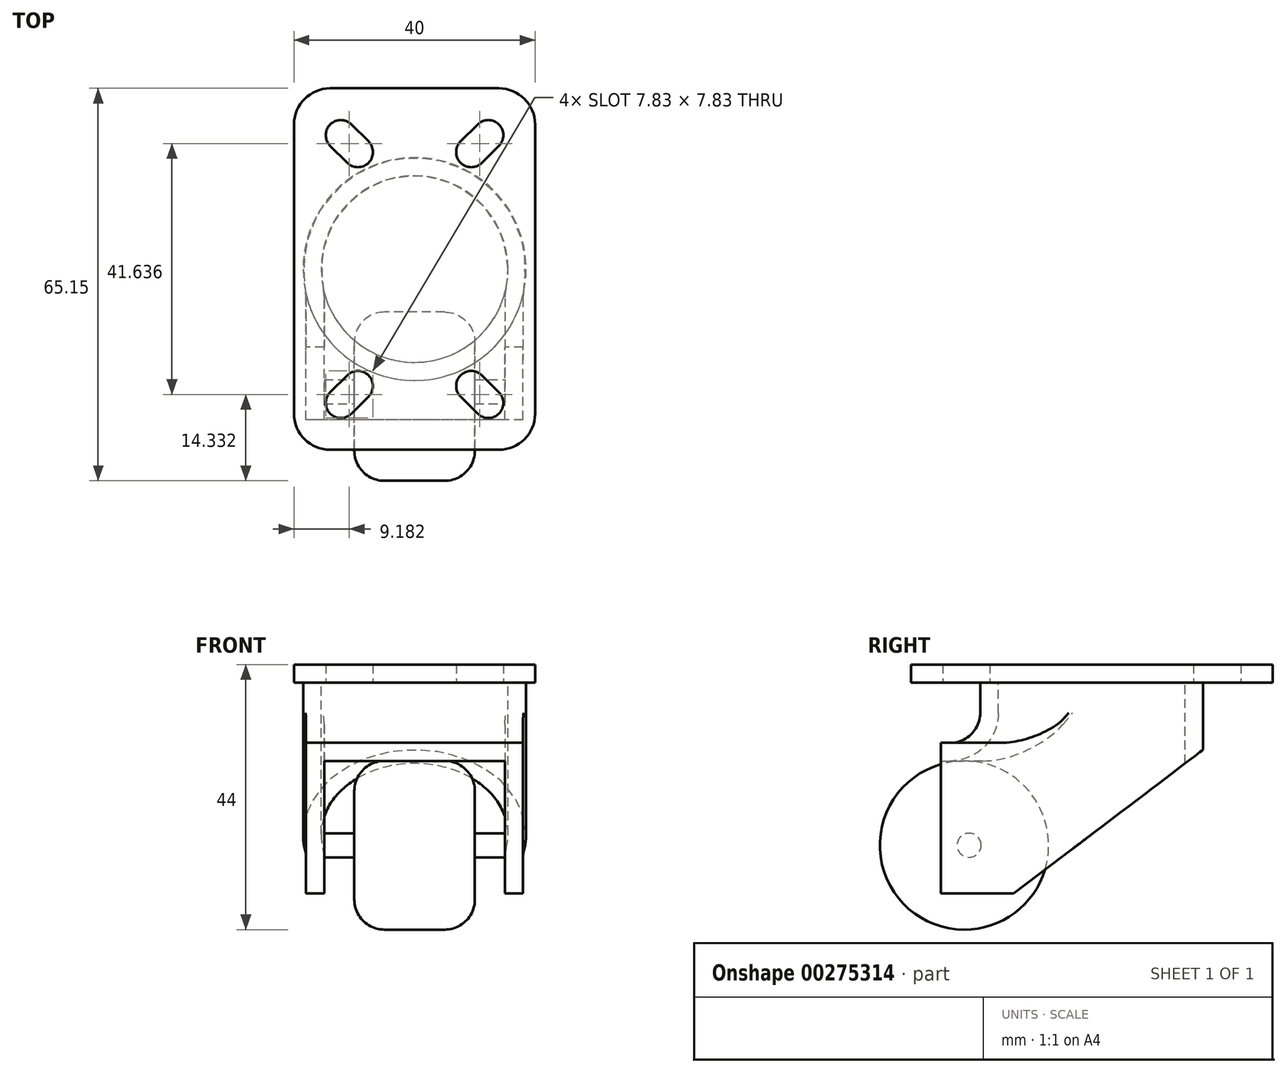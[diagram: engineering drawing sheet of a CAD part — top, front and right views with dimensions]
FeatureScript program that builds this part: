
annotation { "Feature Type Name" : "Feature", "Feature Type Description" : "" }
export const myFeature = defineFeature(function(context is Context, id is Id, definition is map)
    precondition{}
    {
        {
            var Q0;
            Q0=qCreatedBy(makeId("Top.planeOp"),FACE);
            var sketch = newSketch(context, id + "F0", { "sketchPlane" : qUnion([Q0])});
            skLineSegment(sketch, "E0.bottom", {"start": v(14, 30) * mm, "end": v(-14, 30) * mm});
            skLineSegment(sketch, "E0.top", {"start": v(14, -30) * mm, "end": v(-14, -30) * mm});
            skLineSegment(sketch, "E0.left", {"start": v(20, 24) * mm, "end": v(20, -24) * mm});
            skLineSegment(sketch, "E0.right", {"start": v(-20, 24) * mm, "end": v(-20, -24) * mm});
            skPoint(sketch, "E0.middle", {"position": v(0, 0) * mm});
            skPoint(sketch, "E1.visualSharp", {"position": v(-20, 30) * mm});
            skArc(sketch, "E1.filletArc", {"start": v(-14, 30) * mm, "mid": v(-18.24, 28.24) * mm, "end": v(-20, 24) * mm});
            skPoint(sketch, "E2.visualSharp", {"position": v(20, 30) * mm});
            skArc(sketch, "E2.filletArc", {"start": v(20, 24) * mm, "mid": v(18.24, 28.24) * mm, "end": v(14, 30) * mm});
            skPoint(sketch, "E3.visualSharp", {"position": v(-20, -30) * mm});
            skArc(sketch, "E3.filletArc", {"start": v(-20, -24) * mm, "mid": v(-18.24, -28.24) * mm, "end": v(-14, -30) * mm});
            skPoint(sketch, "E4.visualSharp", {"position": v(20, -30) * mm});
            skArc(sketch, "E4.filletArc", {"start": v(14, -30) * mm, "mid": v(18.24, -28.24) * mm, "end": v(20, -24) * mm});
            skLineSegment(sketch, "E5", {"start": v(-14, 24) * mm, "end": v(-14, 24) * mm});
            skLineSegment(sketch, "E6", {"start": v(-14, 20.46) * mm, "end": v(-11.17, 17.64) * mm});
            skLineSegment(sketch, "E7", {"start": v(-10.46, 24) * mm, "end": v(-7.64, 21.17) * mm});
            skLineSegment(sketch, "E8", {"start": v(-7.64, 17.64) * mm, "end": v(-7.64, 17.64) * mm});
            skPoint(sketch, "E9.visualSharp", {"position": v(-15.77, 22.23) * mm});
            skArc(sketch, "E9.filletArc", {"start": v(-14, 24) * mm, "mid": v(-14.73, 22.23) * mm, "end": v(-14, 20.46) * mm});
            skPoint(sketch, "E10.visualSharp", {"position": v(-12.23, 25.77) * mm});
            skArc(sketch, "E10.filletArc", {"start": v(-10.46, 24) * mm, "mid": v(-12.23, 24.73) * mm, "end": v(-14, 24) * mm});
            skPoint(sketch, "E11.visualSharp", {"position": v(-5.87, 19.4) * mm});
            skArc(sketch, "E11.filletArc", {"start": v(-7.64, 17.64) * mm, "mid": v(-6.9, 19.4) * mm, "end": v(-7.64, 21.17) * mm});
            skPoint(sketch, "E12.visualSharp", {"position": v(-9.4, 15.87) * mm});
            skArc(sketch, "E12.filletArc", {"start": v(-11.17, 17.64) * mm, "mid": v(-9.4, 16.9) * mm, "end": v(-7.64, 17.64) * mm});
            skLineSegment(sketch, "E13.MirrorCS", {"start": v(10.46, 24) * mm, "end": v(7.64, 21.17) * mm});
            skArc(sketch, "E14.MirrorCS", {"start": v(7.64, 17.64) * mm, "mid": v(6.9, 19.4) * mm, "end": v(7.64, 21.17) * mm});
            skArc(sketch, "E15.MirrorCS", {"start": v(11.17, 17.64) * mm, "mid": v(9.4, 16.9) * mm, "end": v(7.64, 17.64) * mm});
            skLineSegment(sketch, "E16.MirrorCS", {"start": v(14, 20.46) * mm, "end": v(11.17, 17.64) * mm});
            skArc(sketch, "E17.MirrorCS", {"start": v(14, 24) * mm, "mid": v(14.73, 22.23) * mm, "end": v(14, 20.46) * mm});
            skArc(sketch, "E18.MirrorCS", {"start": v(10.46, 24) * mm, "mid": v(12.23, 24.73) * mm, "end": v(14, 24) * mm});
            skArc(sketch, "E19.MirrorCS", {"start": v(11.17, -17.64) * mm, "mid": v(9.4, -16.9) * mm, "end": v(7.64, -17.64) * mm});
            skArc(sketch, "E20.MirrorCS", {"start": v(7.64, -17.64) * mm, "mid": v(6.9, -19.4) * mm, "end": v(7.64, -21.17) * mm});
            skLineSegment(sketch, "E21.MirrorCS", {"start": v(10.46, -24) * mm, "end": v(7.64, -21.17) * mm});
            skArc(sketch, "E22.MirrorCS", {"start": v(14, -24) * mm, "mid": v(14.73, -22.23) * mm, "end": v(14, -20.46) * mm});
            skArc(sketch, "E23.MirrorCS", {"start": v(10.46, -24) * mm, "mid": v(12.23, -24.73) * mm, "end": v(14, -24) * mm});
            skLineSegment(sketch, "E24.MirrorCS", {"start": v(14, -20.46) * mm, "end": v(11.17, -17.64) * mm});
            skArc(sketch, "E25.MirrorCS", {"start": v(-7.64, -17.64) * mm, "mid": v(-6.9, -19.4) * mm, "end": v(-7.64, -21.17) * mm});
            skArc(sketch, "E26.MirrorCS", {"start": v(-11.17, -17.64) * mm, "mid": v(-9.4, -16.9) * mm, "end": v(-7.64, -17.64) * mm});
            skLineSegment(sketch, "E27.MirrorCS", {"start": v(-14, -20.46) * mm, "end": v(-11.17, -17.64) * mm});
            skArc(sketch, "E28.MirrorCS", {"start": v(-14, -24) * mm, "mid": v(-14.73, -22.23) * mm, "end": v(-14, -20.46) * mm});
            skArc(sketch, "E29.MirrorCS", {"start": v(-10.46, -24) * mm, "mid": v(-12.23, -24.73) * mm, "end": v(-14, -24) * mm});
            skLineSegment(sketch, "E30.MirrorCS", {"start": v(-10.46, -24) * mm, "end": v(-7.64, -21.17) * mm});
            skSolve(sketch);
        }
        {
            var Q0;
            Q0=makeQuery(id+"F0.imprint","IMPRINT",FACE,{"disambiguationData":[TD([[makeQuery(id+"F0.imprint","IMPRINT",EDGE,{"derivedFrom":sQuery(id+"F0.wireOp",EDGE,"E0.bottom")}),1.0]])]});
            extrude(context, id + "F1", {"entities" : qUnion([Q0]), "depth" : 3 * mm});
        }
        {
            var Q0;
            Q0=makeQuery(id+"F1.opExtrude","CAP_FACE",FACE,{"disambiguationData":[OSD([sQuery(id+"F0.wireOp",EDGE,"E0.bottom"),sQuery(id+"F0.wireOp",EDGE,"E0.top"),sQuery(id+"F0.wireOp",EDGE,"E0.left"),sQuery(id+"F0.wireOp",EDGE,"E0.right"),sQuery(id+"F0.wireOp",EDGE,"E1.filletArc"),sQuery(id+"F0.wireOp",EDGE,"E2.filletArc"),sQuery(id+"F0.wireOp",EDGE,"E3.filletArc"),sQuery(id+"F0.wireOp",EDGE,"E4.filletArc"),sQuery(id+"F0.wireOp",EDGE,"E6"),sQuery(id+"F0.wireOp",EDGE,"E7"),sQuery(id+"F0.wireOp",EDGE,"E9.filletArc"),sQuery(id+"F0.wireOp",EDGE,"E10.filletArc"),sQuery(id+"F0.wireOp",EDGE,"E11.filletArc"),sQuery(id+"F0.wireOp",EDGE,"E12.filletArc"),sQuery(id+"F0.wireOp",EDGE,"E13.MirrorCS"),sQuery(id+"F0.wireOp",EDGE,"E14.MirrorCS"),sQuery(id+"F0.wireOp",EDGE,"E15.MirrorCS"),sQuery(id+"F0.wireOp",EDGE,"E16.MirrorCS"),sQuery(id+"F0.wireOp",EDGE,"E17.MirrorCS"),sQuery(id+"F0.wireOp",EDGE,"E18.MirrorCS"),sQuery(id+"F0.wireOp",EDGE,"E19.MirrorCS"),sQuery(id+"F0.wireOp",EDGE,"E20.MirrorCS"),sQuery(id+"F0.wireOp",EDGE,"E22.MirrorCS"),sQuery(id+"F0.wireOp",EDGE,"E23.MirrorCS"),sQuery(id+"F0.wireOp",EDGE,"E21.MirrorCS"),sQuery(id+"F0.wireOp",EDGE,"E24.MirrorCS"),sQuery(id+"F0.wireOp",EDGE,"E25.MirrorCS"),sQuery(id+"F0.wireOp",EDGE,"E26.MirrorCS"),sQuery(id+"F0.wireOp",EDGE,"E27.MirrorCS"),sQuery(id+"F0.wireOp",EDGE,"E28.MirrorCS"),sQuery(id+"F0.wireOp",EDGE,"E29.MirrorCS"),sQuery(id+"F0.wireOp",EDGE,"E30.MirrorCS")])],"isStart":true});
            var sketch = newSketch(context, id + "F2", { "sketchPlane" : qUnion([Q0])});
            skCircle(sketch, "E31", {"center": v(0, 0) * mm, "radius": 18.5 * mm});
            skSolve(sketch);
        }
        {
            var Q0;
            Q0=makeQuery(id+"F2.imprint","IMPRINT",FACE,{"disambiguationData":[TD([[makeQuery(id+"F2.imprint","IMPRINT",EDGE,{"derivedFrom":sQuery(id+"F2.wireOp",EDGE,"E31")}),1.0]])]});
            extrude(context, id + "F3", {"entities" : qUnion([Q0]), "operationType" : NewBodyOperationType.ADD, "depth" : 35 * mm});
        }
        {
            var Q0;
            Q0=qCreatedBy(makeId("Front.planeOp"),FACE);
            var sketch = newSketch(context, id + "F4", { "sketchPlane" : qUnion([Q0])});
            skLineSegment(sketch, "E32.bottom", {"start": v(0, -10) * mm, "end": v(-18, -10) * mm});
            skLineSegment(sketch, "E32.top", {"start": v(0, -35) * mm, "end": v(-18, -35) * mm});
            skLineSegment(sketch, "E32.left", {"start": v(0, -10) * mm, "end": v(0, -35) * mm});
            skLineSegment(sketch, "E32.right", {"start": v(-18, -10) * mm, "end": v(-18, -35) * mm});
            skLineSegment(sketch, "E33.MirrorCS", {"start": v(0, -10) * mm, "end": v(18, -10) * mm});
            skLineSegment(sketch, "E34.MirrorCS", {"start": v(18, -10) * mm, "end": v(18, -35) * mm});
            skLineSegment(sketch, "E35.MirrorCS", {"start": v(0, -35) * mm, "end": v(18, -35) * mm});
            skSolve(sketch);
        }
        {
            var Q0;
            Q0=makeQuery(id+"F4.imprint","IMPRINT",FACE,{"disambiguationData":[TD([[makeQuery(id+"F4.imprint","IMPRINT",EDGE,{"derivedFrom":sQuery(id+"F4.wireOp",EDGE,"E32.bottom")}),1.0]])]});
            var Q1;
            Q1=makeQuery(id+"F4.imprint","IMPRINT",FACE,{"disambiguationData":[TD([[makeQuery(id+"F4.imprint","IMPRINT",EDGE,{"derivedFrom":sQuery(id+"F4.wireOp",EDGE,"E32.left")}),1.0]])]});
            extrude(context, id + "F5", {"entities" : qUnion([Q0, Q1]), "operationType" : NewBodyOperationType.ADD, "depth" : 25 * mm});
        }
        {
            var Q0;
            Q0=makeQuery(id+"F5.boolean.opBoolean","INTERSECT",EDGE,{"derivedFrom":[makeQuery(id+"F3.opExtrude","SWEPT_FACE",FACE,{"disambiguationData":[OSD([sQuery(id+"F2.wireOp",EDGE,"E31")])]}),makeQuery(id+"F5.opExtrude","SWEPT_FACE",FACE,{"disambiguationData":[OSD([sQuery(id+"F4.wireOp",EDGE,"E32.bottom"),sQuery(id+"F4.wireOp",EDGE,"E33.MirrorCS")])]})]});
            fillet(context, id + "F6", {"entities" : qUnion([Q0]), "radius" : 5 * mm, "tangentPropagation" : true, "allowEdgeOverflow" : false});
        }
        {
            var Q0;
            Q0=makeQuery(id+"F5.boolean.opBoolean","INTERSECT",EDGE,{"derivedFrom":[makeQuery(id+"F3.opExtrude","SWEPT_FACE",FACE,{"disambiguationData":[OSD([sQuery(id+"F2.wireOp",EDGE,"E31")])]}),makeQuery(id+"F5.opExtrude","SWEPT_FACE",FACE,{"disambiguationData":[OSD([sQuery(id+"F4.wireOp",EDGE,"E32.right")])]})]});
            fillet(context, id + "F7", {"entities" : qUnion([Q0]), "radius" : 5 * mm, "tangentPropagation" : true, "allowEdgeOverflow" : false});
        }
        {
            var Q0;
            Q0=makeQuery(id+"F5.boolean.opBoolean","INTERSECT",EDGE,{"derivedFrom":[makeQuery(id+"F3.opExtrude","SWEPT_FACE",FACE,{"disambiguationData":[OSD([sQuery(id+"F2.wireOp",EDGE,"E31")])]}),makeQuery(id+"F5.opExtrude","SWEPT_FACE",FACE,{"disambiguationData":[OSD([sQuery(id+"F4.wireOp",EDGE,"E34.MirrorCS")])]})]});
            fillet(context, id + "F8", {"entities" : qUnion([Q0]), "radius" : 5 * mm, "tangentPropagation" : true, "allowEdgeOverflow" : false});
        }
        {
            var Q0;
            Q0=qCreatedBy(makeId("Right.planeOp"),FACE);
            var sketch = newSketch(context, id + "F9", { "sketchPlane" : qUnion([Q0])});
            skLineSegment(sketch, "E36", {"start": v(19.85, -10.11) * mm, "end": v(-23.19, -42.76) * mm});
            skLineSegment(sketch, "E37", {"start": v(-23.19, -42.76) * mm, "end": v(19.85, -42.76) * mm});
            skLineSegment(sketch, "E38", {"start": v(19.85, -42.76) * mm, "end": v(19.85, -10.11) * mm});
            skSolve(sketch);
        }
        {
            var Q0;
            Q0=qSketchRegion(id+"F9",true);
            extrude(context, id + "F10", {"entities" : qUnion([Q0]), "operationType" : NewBodyOperationType.REMOVE, "oppositeDirection" : true, "depth" : 25 * mm, "hasSecondDirection" : true, "secondDirectionOppositeDirection" : false, "secondDirectionDepth" : 25 * mm});
        }
        {
            var Q0;
            Q0=makeQuery(id+"F10.boolean.opBoolean","COPY",FACE,{"derivedFrom":makeQuery(id+"F10.opExtrude","SWEPT_FACE",FACE,{"disambiguationData":[OSD([sQuery(id+"F9.wireOp",EDGE,"E36")])]})});
            var Q1;
            Q1=makeQuery(id+"F5.opExtrude","SWEPT_FACE",FACE,{"disambiguationData":[OSD([sQuery(id+"F4.wireOp",EDGE,"E32.top"),sQuery(id+"F4.wireOp",EDGE,"E35.MirrorCS")])]});
            var Q2;
            Q2=makeQuery(id+"F5.opExtrude","CAP_FACE",FACE,{"disambiguationData":[OSD([sQuery(id+"F4.wireOp",EDGE,"E32.bottom"),sQuery(id+"F4.wireOp",EDGE,"E32.top"),sQuery(id+"F4.wireOp",EDGE,"E32.right"),sQuery(id+"F4.wireOp",EDGE,"E33.MirrorCS"),sQuery(id+"F4.wireOp",EDGE,"E34.MirrorCS"),sQuery(id+"F4.wireOp",EDGE,"E35.MirrorCS")])],"isStart":false});
            shell(context, id + "F11", {"entities" : qUnion([Q0, Q1, Q2]), "thickness" : 3 * mm});
        }
        {
            var Q0;
            Q0=makeQuery(id+"F5.opExtrude","SWEPT_FACE",FACE,{"disambiguationData":[OSD([sQuery(id+"F4.wireOp",EDGE,"E34.MirrorCS")])]});
            var sketch = newSketch(context, id + "F12", { "sketchPlane" : qUnion([Q0])});
            skCircle(sketch, "E39", {"center": v(-20.35, -27) * mm, "radius": 2 * mm});
            skSolve(sketch);
        }
        {
            var Q0;
            Q0=makeQuery(id+"F12.imprint","IMPRINT",FACE,{"disambiguationData":[TD([[makeQuery(id+"F12.imprint","IMPRINT",EDGE,{"derivedFrom":sQuery(id+"F12.wireOp",EDGE,"E39")}),1.0]])]});
            var Q1;
            Q1=makeQuery(id+"F5.opExtrude","SWEPT_FACE",FACE,{"disambiguationData":[OSD([sQuery(id+"F4.wireOp",EDGE,"E32.right")])]});
            extrude(context, id + "F13", {"entities" : qUnion([Q0]), "operationType" : NewBodyOperationType.ADD, "endBound" : BoundingType.UP_TO_SURFACE, "oppositeDirection" : true, "endBoundEntityFace" : qUnion([Q1]), "depth" : 25 * mm});
        }
        {
            var Q0;
            Q0=qCreatedBy(makeId("Right.planeOp"),FACE);
            var sketch = newSketch(context, id + "F14", { "sketchPlane" : qUnion([Q0])});
            skCircle(sketch, "E40", {"center": v(-21.15, -27) * mm, "radius": 14 * mm});
            skSolve(sketch);
        }
        {
            var Q0;
            Q0=makeQuery(id+"F14.imprint","IMPRINT",FACE,{"disambiguationData":[TD([[makeQuery(id+"F14.imprint","IMPRINT",EDGE,{"derivedFrom":sQuery(id+"F14.wireOp",EDGE,"E40")}),1.0]])]});
            extrude(context, id + "F15", {"entities" : qUnion([Q0]), "operationType" : NewBodyOperationType.ADD, "depth" : 10 * mm, "hasSecondDirection" : true, "secondDirectionOppositeDirection" : true, "secondDirectionDepth" : 10 * mm});
        }
        {
            var Q0;
            Q0=makeQuery(id+"F15.opExtrude","CAP_EDGE",EDGE,{"disambiguationData":[OSD([sQuery(id+"F14.wireOp",EDGE,"E40")])],"isStart":false});
            var Q1;
            Q1=makeQuery(id+"F15.opExtrude","CAP_EDGE",EDGE,{"disambiguationData":[OSD([sQuery(id+"F14.wireOp",EDGE,"E40")])],"isStart":true});
            fillet(context, id + "F16", {"entities" : qUnion([Q0, Q1]), "radius" : 5 * mm, "tangentPropagation" : true, "allowEdgeOverflow" : false});
        }
    });
